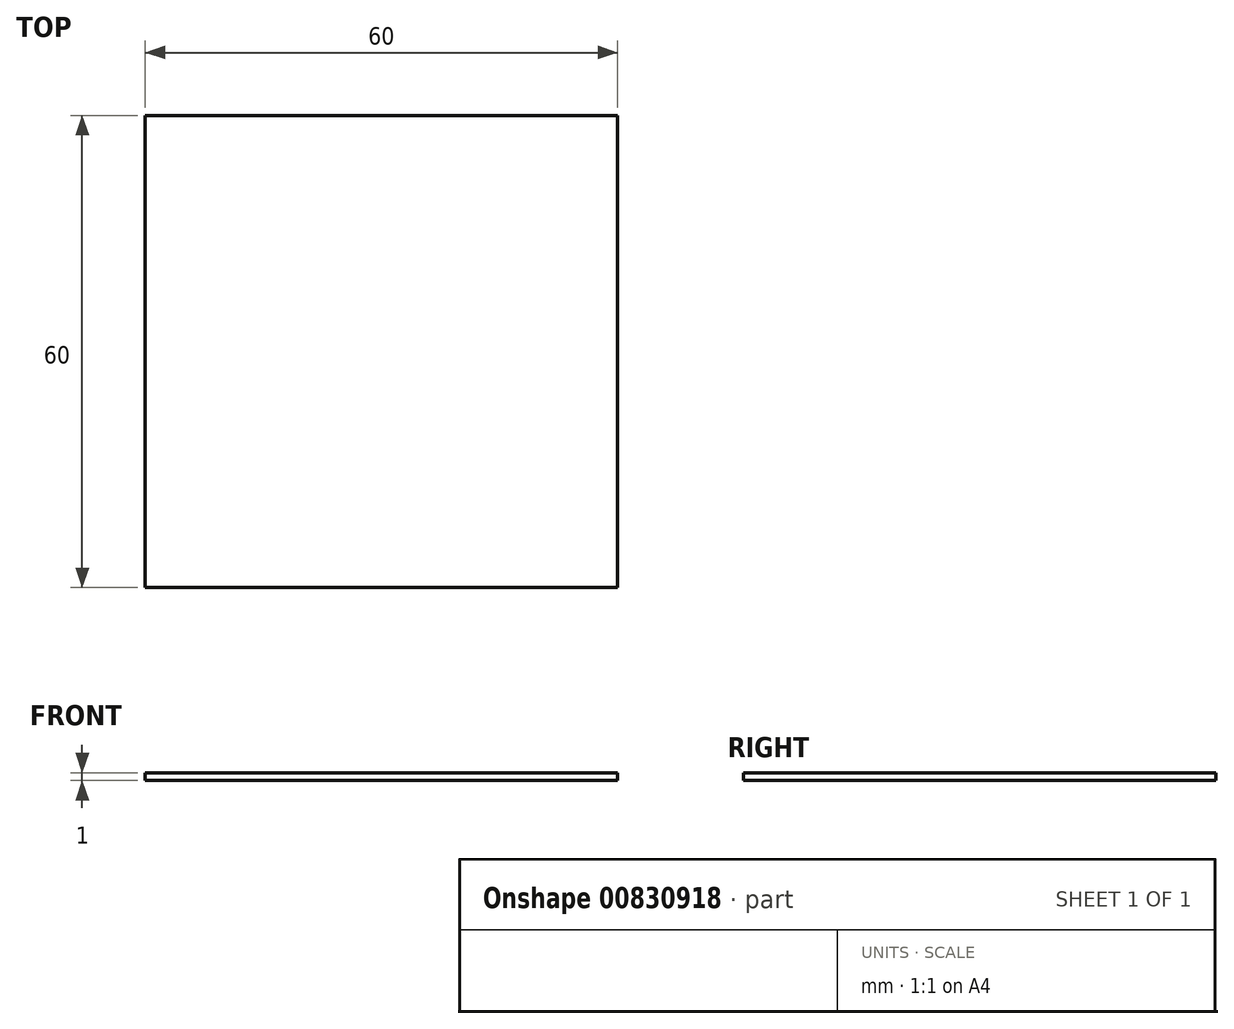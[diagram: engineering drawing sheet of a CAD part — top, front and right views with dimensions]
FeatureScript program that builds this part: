
annotation { "Feature Type Name" : "Feature", "Feature Type Description" : "" }
export const myFeature = defineFeature(function(context is Context, id is Id, definition is map)
    precondition{}
    {
        {
            var Q0;
            Q0=qCreatedBy(makeId("Top.planeOp"),FACE);
            var sketch = newSketch(context, id + "F0", { "sketchPlane" : qUnion([Q0])});
            skLineSegment(sketch, "E0.bottom", {"start": v(0, 0) * mm, "end": v(60, 0) * mm});
            skLineSegment(sketch, "E0.top", {"start": v(0, 60) * mm, "end": v(60, 60) * mm});
            skLineSegment(sketch, "E0.left", {"start": v(0, 0) * mm, "end": v(0, 60) * mm});
            skLineSegment(sketch, "E0.right", {"start": v(60, 0) * mm, "end": v(60, 60) * mm});
            skSolve(sketch);
        }
        {
            var Q0;
            Q0 = qSketchRegion(id + "F0", true);
            extrude(context, id + "F1", {"entities" : qUnion([Q0]), "depth" : 1 * mm, "offsetDistance" : 25 * mm});
        }
    });
